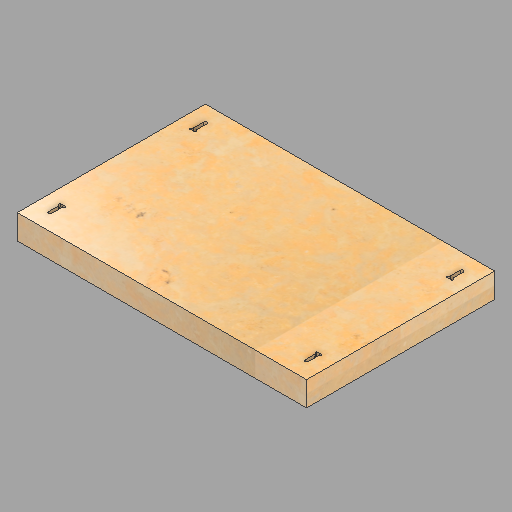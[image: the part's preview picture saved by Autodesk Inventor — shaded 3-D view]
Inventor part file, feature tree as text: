
AUTODESK INVENTOR PART (.ipt)
format: ipt  version: 2023 (Build 270158000, 158)  size: 484,352 bytes
history: native  units: in
note: dims shown in document units (in); Inventor stores cm internally (conversion verified against a paired STEP export)
features: other x14, revolve x6, sketch x4, extrude x1, plane x1, split x1, move_body x1, boolean_combine x1, projected_geometry x1
ambient origin geometry x8: Origin, YZ Plane, XZ Plane, XY Plane, X Axis, Y Axis, Z Axis, Center Point
bodies: Solid1 (feature_tree), Solid2 (feature_tree), Solid3 (feature_tree)
feature tree (30):
  other  "Blocks"
  extrude  "Extrusion1"  Depth=23.0in
  sketch  "Sketch2"  dims[d2=47.375in d3=0.0in d4=2.0in]
  revolve  "Revolution1"  [1 undecoded]
  revolve  "Revolution2"  Angle=90.0deg
  sketch  "Sketch3"  dims[d5=1.0in d6=90.0deg]
  revolve  "Revolution3"  Angle=90.0deg
  revolve  "Revolution4"  Angle=90.0deg
  sketch  "Sketch4"  dims[d7=90.0deg d8=90.0deg d9=90.0deg d10=90.0deg d11=90.0deg d12=-12.0in d13=0.0in d14=0.0in]
  revolve  "Revolution5"  Angle=90.0deg
  revolve  "Revolution6"  Angle=90.0deg
  plane  "Work Plane1"
  split  "Split1"
  move_body  "Move Body1"
  boolean_combine  "Combine1"
  sketch  "Sketch1"  dims[d0=2.0in d1=23.0in]
  projected_geometry  "Projected Loop1"
  other  "Bolt"
  other  "Block2"
  other  "Block3"
  other  "Block2:1"
  other  "Bolt:2"
  other  "Block2:2"
  other  "Block2:4"
  other  "Block3:1"
  other  "Block3:2"
  other  "Block3:3"
  other  "Block3:4"
  other  "Block3:5"
  other  "Block3:6"
note: 1 required parameter value undecoded (feature->parameter linkage not recoverable at this tier; creation-order binding heuristic only, values carry confidence <= 0.55)
